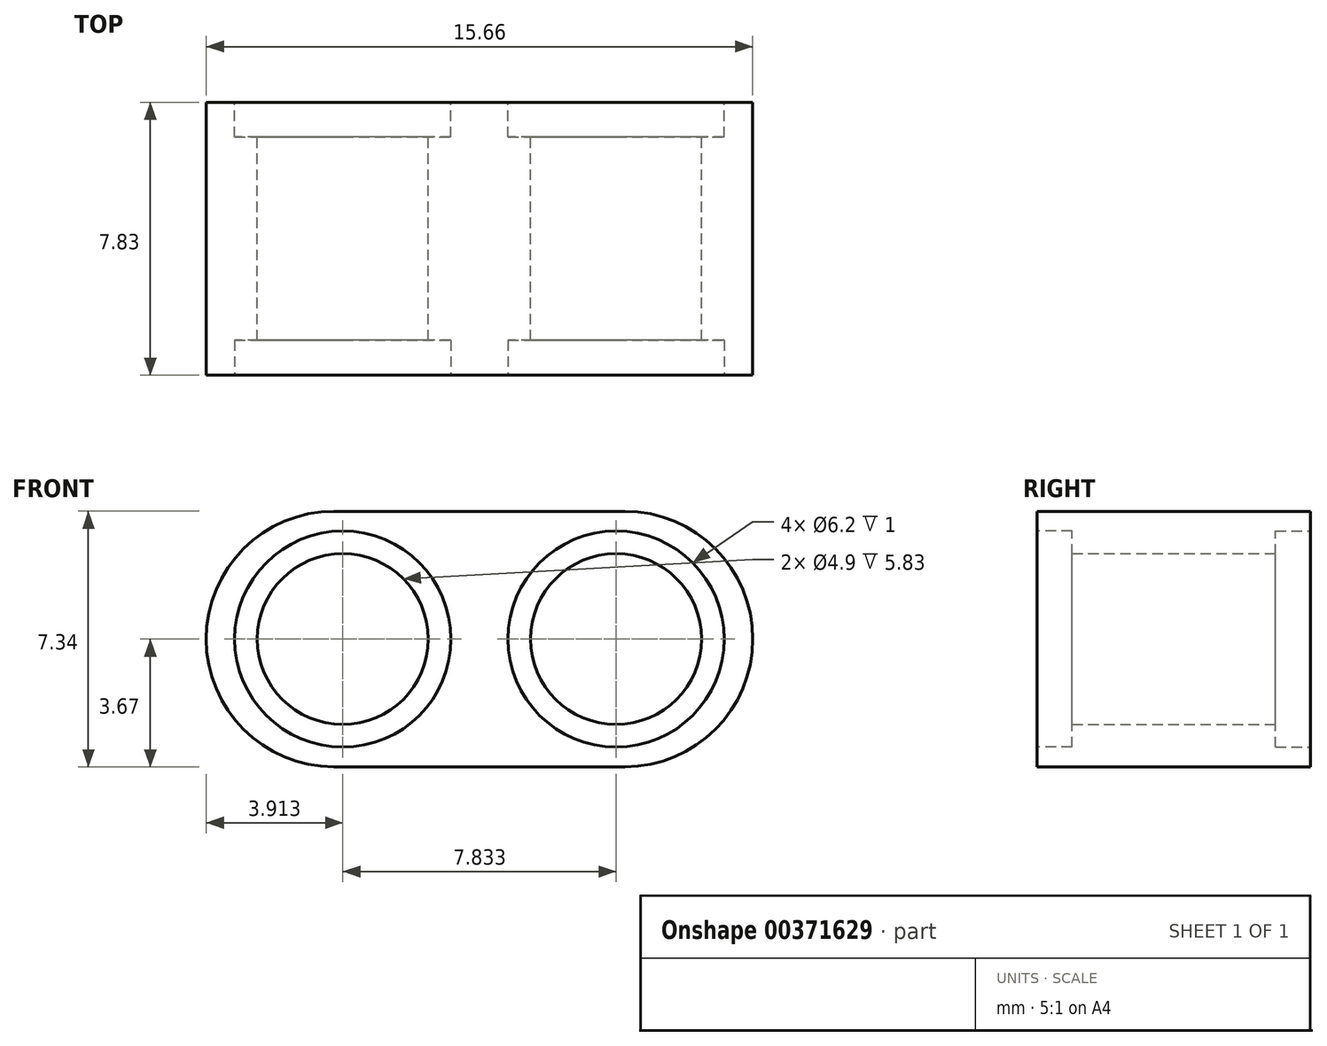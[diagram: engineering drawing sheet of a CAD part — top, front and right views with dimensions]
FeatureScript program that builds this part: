
annotation { "Feature Type Name" : "Feature", "Feature Type Description" : "" }
export const myFeature = defineFeature(function(context is Context, id is Id, definition is map)
    precondition{}
    {
        {
            var Q0;
            Q0=qCreatedBy(makeId("Front.planeOp"),FACE);
            var sketch = newSketch(context, id + "F0", { "sketchPlane" : qUnion([Q0])});
            skLineSegment(sketch, "E0", {"start": v(-0.49, -3.67) * mm, "end": v(7.85, -3.67) * mm});
            skLineSegment(sketch, "E1", {"start": v(11.51, -3.67) * mm, "end": v(3.68, -3.67) * mm, "construction": true});
            skLineSegment(sketch, "E2", {"start": v(11.51, 0) * mm, "end": v(11.51, 0) * mm});
            skLineSegment(sketch, "E3", {"start": v(-11.99, 0) * mm, "end": v(11.51, 0) * mm, "construction": true});
            skLineSegment(sketch, "E4", {"start": v(7.85, 3.67) * mm, "end": v(3.68, 3.67) * mm});
            skLineSegment(sketch, "E5", {"start": v(3.68, 3.67) * mm, "end": v(-0.49, 3.67) * mm});
            skLineSegment(sketch, "E6", {"start": v(-11.99, 0) * mm, "end": v(-11.99, 0) * mm});
            skLineSegment(sketch, "E7", {"start": v(3.68, 3.67) * mm, "end": v(3.68, -3.67) * mm, "construction": true});
            skLineSegment(sketch, "E8", {"start": v(-8.07, -3.67) * mm, "end": v(-8.07, 3.67) * mm, "construction": true});
            skLineSegment(sketch, "E9", {"start": v(-0.24, 3.67) * mm, "end": v(-0.24, -3.67) * mm, "construction": true});
            skLineSegment(sketch, "E10", {"start": v(7.6, 3.67) * mm, "end": v(7.6, -3.67) * mm, "construction": true});
            skPoint(sketch, "E11.visualSharp", {"position": v(-11.99, 3.67) * mm});
            skPoint(sketch, "E12.visualSharp", {"position": v(-11.99, -3.67) * mm});
            skPoint(sketch, "E13.visualSharp", {"position": v(11.51, 3.67) * mm});
            skArc(sketch, "E13.filletArc", {"start": v(11.51, 0) * mm, "mid": v(10.44, 2.6) * mm, "end": v(7.85, 3.66) * mm});
            skPoint(sketch, "E14.visualSharp", {"position": v(11.51, -3.67) * mm});
            skArc(sketch, "E14.filletArc", {"start": v(7.85, -3.67) * mm, "mid": v(10.44, -2.6) * mm, "end": v(11.51, 0) * mm});
            skCircle(sketch, "E15", {"center": v(7.6, 0) * mm, "radius": 2.45 * mm});
            skCircle(sketch, "E16", {"center": v(-0.24, 0) * mm, "radius": 2.45 * mm});
            skArc(sketch, "E17", {"start": v(-1.82, 2.67) * mm, "mid": v(-3.34, 0) * mm, "end": v(-1.82, -2.67) * mm});
            skArc(sketch, "E18", {"start": v(-1.82, -2.67) * mm, "mid": v(-0.24, -3.1) * mm, "end": v(1.35, -2.67) * mm});
            skArc(sketch, "E19", {"start": v(1.35, 2.67) * mm, "mid": v(-0.24, 3.1) * mm, "end": v(-1.82, 2.67) * mm});
            skArc(sketch, "E20", {"start": v(1.35, -2.67) * mm, "mid": v(2.86, 0) * mm, "end": v(1.35, 2.67) * mm});
            skArc(sketch, "E21", {"start": v(6.01, 2.67) * mm, "mid": v(4.5, 0) * mm, "end": v(6.01, -2.67) * mm});
            skArc(sketch, "E22", {"start": v(6.01, -2.67) * mm, "mid": v(10.7, 0) * mm, "end": v(6.01, 2.67) * mm});
            skLineSegment(sketch, "E23", {"start": v(-4.15, 0) * mm, "end": v(-4.15, 0) * mm});
            skPoint(sketch, "E24.newPointB", {"position": v(-4.15, -3.67) * mm});
            skArc(sketch, "E24.filletArc", {"start": v(-4.15, 0) * mm, "mid": v(-3.08, -2.6) * mm, "end": v(-0.49, -3.67) * mm});
            skPoint(sketch, "E25.visualSharp", {"position": v(-4.15, 3.67) * mm});
            skArc(sketch, "E25.filletArc", {"start": v(-0.49, 3.67) * mm, "mid": v(-3.08, 2.6) * mm, "end": v(-4.15, 0) * mm});
            skSolve(sketch);
        }
        {
            var Q0;
            Q0=makeQuery(id+"F0.imprint","IMPRINT",FACE,{"disambiguationData":[TD([[makeQuery(id+"F0.imprint","IMPRINT",EDGE,{"derivedFrom":sQuery(id+"F0.wireOp",EDGE,"E16")}),-1.0]])]});
            var Q1;
            Q1=makeQuery(id+"F0.imprint","IMPRINT",FACE,{"disambiguationData":[TD([[makeQuery(id+"F0.imprint","IMPRINT",EDGE,{"derivedFrom":sQuery(id+"F0.wireOp",EDGE,"E15")}),-1.0]])]});
            var Q2;
            Q2=makeQuery(id+"F0.imprint","IMPRINT",FACE,{"disambiguationData":[TD([[makeQuery(id+"F0.imprint","IMPRINT",EDGE,{"derivedFrom":sQuery(id+"F0.wireOp",EDGE,"E0")}),1.0]])]});
            extrude(context, id + "F1", {"entities" : qUnion([Q0, Q1, Q2]), "depth" : 7.83 * mm});
        }
        {
            var Q0;
            Q0=makeQuery(id+"F0.imprint","IMPRINT",FACE,{"disambiguationData":[TD([[makeQuery(id+"F0.imprint","IMPRINT",EDGE,{"derivedFrom":sQuery(id+"F0.wireOp",EDGE,"E16")}),-1.0]])]});
            var Q1;
            Q1=makeQuery(id+"F0.imprint","IMPRINT",FACE,{"disambiguationData":[TD([[makeQuery(id+"F0.imprint","IMPRINT",EDGE,{"derivedFrom":sQuery(id+"F0.wireOp",EDGE,"E15")}),-1.0]])]});
            extrude(context, id + "F2", {"entities" : qUnion([Q0, Q1]), "operationType" : NewBodyOperationType.REMOVE, "depth" : 1 * mm});
        }
        {
            var Q0;
            Q0=makeQuery(id+"F1.opExtrude","CAP_FACE",FACE,{"disambiguationData":[OSD([sQuery(id+"F0.wireOp",EDGE,"E0"),sQuery(id+"F0.wireOp",EDGE,"E4"),sQuery(id+"F0.wireOp",EDGE,"E5"),sQuery(id+"F0.wireOp",EDGE,"E13.filletArc"),sQuery(id+"F0.wireOp",EDGE,"E14.filletArc"),sQuery(id+"F0.wireOp",EDGE,"E15"),sQuery(id+"F0.wireOp",EDGE,"E16"),sQuery(id+"F0.wireOp",EDGE,"E24.filletArc"),sQuery(id+"F0.wireOp",EDGE,"E25.filletArc")])],"isStart":false});
            var sketch = newSketch(context, id + "F3", { "sketchPlane" : qUnion([Q0])});
            skCircle(sketch, "E26", {"center": v(-0.24, 0) * mm, "radius": 3.1 * mm});
            skCircle(sketch, "E27", {"center": v(7.6, 0) * mm, "radius": 3.1 * mm});
            skSolve(sketch);
        }
        {
            var Q0;
            Q0=makeQuery(id+"F3.imprint","IMPRINT",FACE,{"disambiguationData":[TD([[makeQuery(id+"F3.imprint","IMPRINT",EDGE,{"derivedFrom":sQuery(id+"F3.wireOp",EDGE,"E26")}),1.0]])]});
            var Q1;
            Q1=makeQuery(id+"F3.imprint","IMPRINT",FACE,{"disambiguationData":[TD([[makeQuery(id+"F3.imprint","IMPRINT",EDGE,{"derivedFrom":sQuery(id+"F3.wireOp",EDGE,"E27")}),1.0]])]});
            extrude(context, id + "F4", {"entities" : qUnion([Q0, Q1]), "operationType" : NewBodyOperationType.REMOVE, "oppositeDirection" : true, "depth" : 1 * mm});
        }
    });
